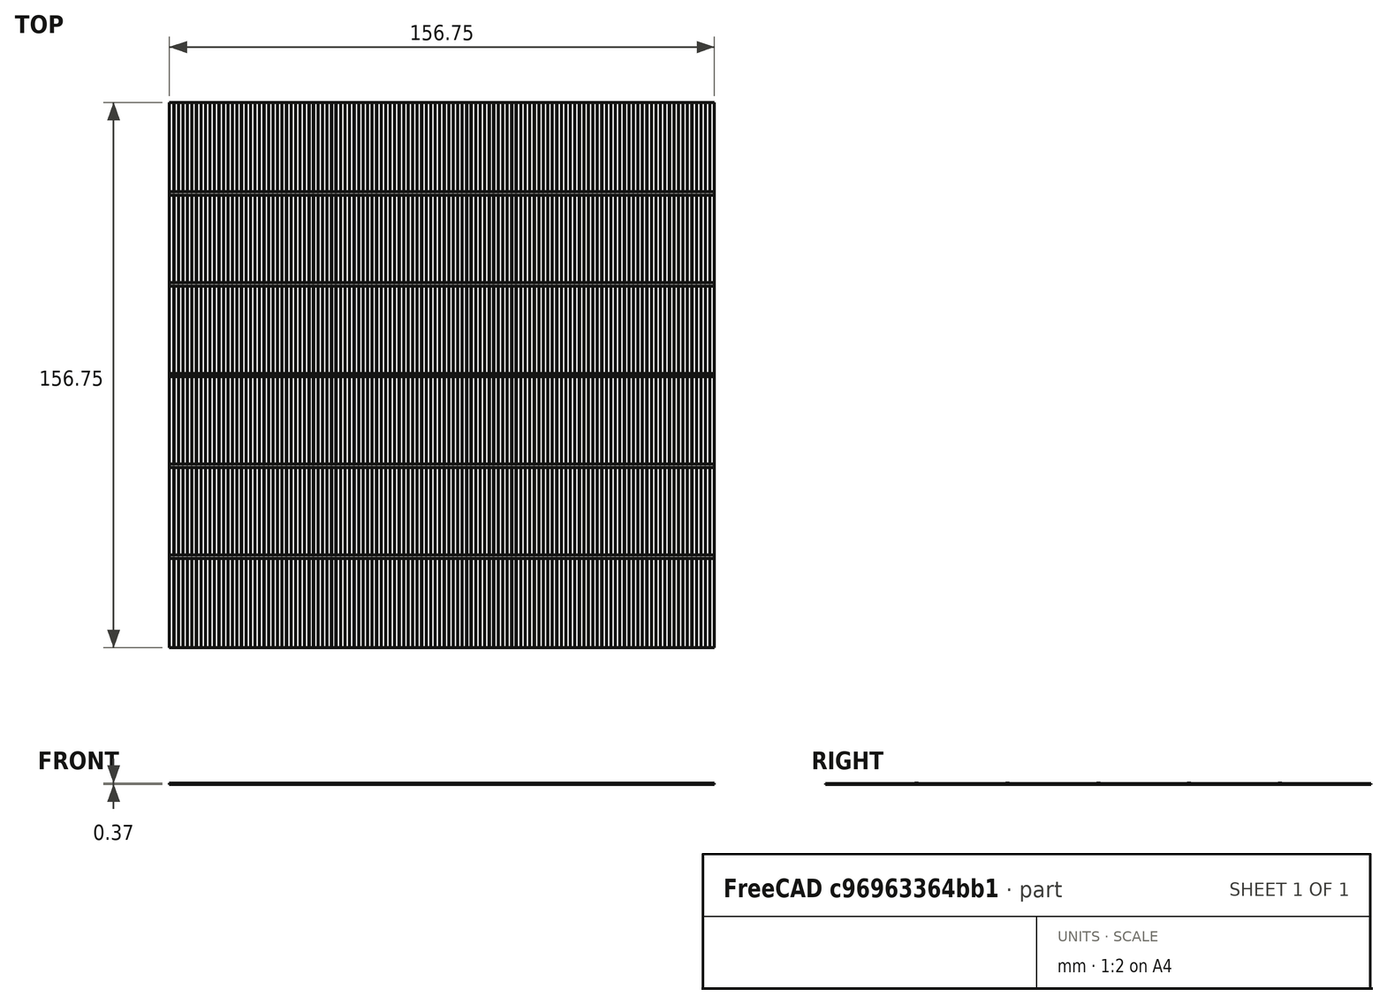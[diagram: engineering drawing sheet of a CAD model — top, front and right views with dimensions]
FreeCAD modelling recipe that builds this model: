
FCSTD DOCUMENT  (FreeCAD 0.19R24276 (Git))
Label: PV_cell
License: All rights reserved
LicenseURL: http://en.wikipedia.org/wiki/All_rights_reserved
objects: Part::Box×128, Part::Feature×6
note: 134 computed .brp shape members not serialized (recipe doc carries the construction recipe); baked Part::Feature solids carry a one-line shape summary decoded from their .brp

FEATURE [Part::Box] Box_Rear_R  label="Box_Rear_R(Box_Rear_R_mat)"
  AttacherType = Attacher::AttachEngine3D
  Height = 1e-05
  Length = 156.75
  Width = 156.75
FEATURE [Part::Feature] Layer_Rear_R  label="Layer_Rear_R(Layer_Rear_R_mat)"
  shape: bbox 156.8 x 156.8 x 2e-07 mm, 1 faces, 0 solids (baked)
FEATURE [Part::Box] Box_Cell  label="Glass_ARC(Box_Cell_mat)"
  AttacherType = Attacher::AttachEngine3D
  Height = 0.17
  Length = 156.75
  Placement = pos=(0,0,1e-05) rot=(0,0,1;0rad)
  Width = 156.75
FEATURE [Part::Box] Box_Front_ARC  label="Box_Front_ARC(Box_Front_ARC_mat)"
  AttacherType = Attacher::AttachEngine3D
  Height = 7.4e-05
  Length = 156.75
  Placement = pos=(0,0,0.17001) rot=(0,0,1;0rad)
  Width = 156.75
FEATURE [Part::Box] Box_Connector_1  label="Box_Connector_1(Box_Connector_mat)"
  AttacherType = Attacher::AttachEngine3D
  Height = 0.2
  Length = 156.75
  Placement = pos=(0,25.625,0.170084) rot=(0,0,1;0rad)
  Width = 1
FEATURE [Part::Box] Box_Connector_2  label="Box_Connector_2(Box_Connector_mat)"
  AttacherType = Attacher::AttachEngine3D
  Height = 0.2
  Length = 156.75
  Placement = pos=(0,51.75,0.170084) rot=(0,0,1;0rad)
  Width = 1
FEATURE [Part::Box] Box_Connector_3  label="Box_Connector_3(Box_Connector_mat)"
  AttacherType = Attacher::AttachEngine3D
  Height = 0.2
  Length = 156.75
  Placement = pos=(0,77.875,0.170084) rot=(0,0,1;0rad)
  Width = 1
FEATURE [Part::Box] Box_Connector_4  label="Box_Connector_4(Box_Connector_mat)"
  AttacherType = Attacher::AttachEngine3D
  Height = 0.2
  Length = 156.75
  Placement = pos=(0,104,0.170084) rot=(0,0,1;0rad)
  Width = 1
FEATURE [Part::Box] Box_Connector_5  label="Box_Connector_5(Box_Connector_mat)"
  AttacherType = Attacher::AttachEngine3D
  Height = 0.2
  Length = 156.75
  Placement = pos=(0,130.125,0.170084) rot=(0,0,1;0rad)
  Width = 1
FEATURE [Part::Box] Box_Finger_1  label="Box_Finger_1(Box_Finger_mat)"
  AttacherType = Attacher::AttachEngine3D
  Height = 0.02
  Length = 0.035
  Placement = pos=(1.27795,0,0.170084) rot=(0,0,1;0rad)
  Width = 156.75
FEATURE [Part::Box] Box_Finger_2  label="Box_Finger_2(Box_Finger_mat)"
  AttacherType = Attacher::AttachEngine3D
  Height = 0.02
  Length = 0.035
  Placement = pos=(2.57341,0,0.170084) rot=(0,0,1;0rad)
  Width = 156.75
FEATURE [Part::Box] Box_Finger_3  label="Box_Finger_3(Box_Finger_mat)"
  AttacherType = Attacher::AttachEngine3D
  Height = 0.02
  Length = 0.035
  Placement = pos=(3.86886,0,0.170084) rot=(0,0,1;0rad)
  Width = 156.75
FEATURE [Part::Box] Box_Finger_4  label="Box_Finger_4(Box_Finger_mat)"
  AttacherType = Attacher::AttachEngine3D
  Height = 0.02
  Length = 0.035
  Placement = pos=(5.16432,0,0.170084) rot=(0,0,1;0rad)
  Width = 156.75
FEATURE [Part::Box] Box_Finger_5  label="Box_Finger_5(Box_Finger_mat)"
  AttacherType = Attacher::AttachEngine3D
  Height = 0.02
  Length = 0.035
  Placement = pos=(6.45977,0,0.170084) rot=(0,0,1;0rad)
  Width = 156.75
FEATURE [Part::Box] Box_Finger_6  label="Box_Finger_6(Box_Finger_mat)"
  AttacherType = Attacher::AttachEngine3D
  Height = 0.02
  Length = 0.035
  Placement = pos=(7.75523,0,0.170084) rot=(0,0,1;0rad)
  Width = 156.75
FEATURE [Part::Box] Box_Finger_7  label="Box_Finger_7(Box_Finger_mat)"
  AttacherType = Attacher::AttachEngine3D
  Height = 0.02
  Length = 0.035
  Placement = pos=(9.05068,0,0.170084) rot=(0,0,1;0rad)
  Width = 156.75
FEATURE [Part::Box] Box_Finger_8  label="Box_Finger_8(Box_Finger_mat)"
  AttacherType = Attacher::AttachEngine3D
  Height = 0.02
  Length = 0.035
  Placement = pos=(10.3461,0,0.170084) rot=(0,0,1;0rad)
  Width = 156.75
FEATURE [Part::Box] Box_Finger_9  label="Box_Finger_9(Box_Finger_mat)"
  AttacherType = Attacher::AttachEngine3D
  Height = 0.02
  Length = 0.035
  Placement = pos=(11.6416,0,0.170084) rot=(0,0,1;0rad)
  Width = 156.75
FEATURE [Part::Box] Box_Finger_10  label="Box_Finger_10(Box_Finger_mat)"
  AttacherType = Attacher::AttachEngine3D
  Height = 0.02
  Length = 0.035
  Placement = pos=(12.937,0,0.170084) rot=(0,0,1;0rad)
  Width = 156.75
FEATURE [Part::Box] Box_Finger_11  label="Box_Finger_11(Box_Finger_mat)"
  AttacherType = Attacher::AttachEngine3D
  Height = 0.02
  Length = 0.035
  Placement = pos=(14.2325,0,0.170084) rot=(0,0,1;0rad)
  Width = 156.75
FEATURE [Part::Box] Box_Finger_12  label="Box_Finger_12(Box_Finger_mat)"
  AttacherType = Attacher::AttachEngine3D
  Height = 0.02
  Length = 0.035
  Placement = pos=(15.528,0,0.170084) rot=(0,0,1;0rad)
  Width = 156.75
FEATURE [Part::Box] Box_Finger_13  label="Box_Finger_13(Box_Finger_mat)"
  AttacherType = Attacher::AttachEngine3D
  Height = 0.02
  Length = 0.035
  Placement = pos=(16.8234,0,0.170084) rot=(0,0,1;0rad)
  Width = 156.75
FEATURE [Part::Box] Box_Finger_14  label="Box_Finger_14(Box_Finger_mat)"
  AttacherType = Attacher::AttachEngine3D
  Height = 0.02
  Length = 0.035
  Placement = pos=(18.1189,0,0.170084) rot=(0,0,1;0rad)
  Width = 156.75
FEATURE [Part::Box] Box_Finger_15  label="Box_Finger_15(Box_Finger_mat)"
  AttacherType = Attacher::AttachEngine3D
  Height = 0.02
  Length = 0.035
  Placement = pos=(19.4143,0,0.170084) rot=(0,0,1;0rad)
  Width = 156.75
FEATURE [Part::Box] Box_Finger_16  label="Box_Finger_16(Box_Finger_mat)"
  AttacherType = Attacher::AttachEngine3D
  Height = 0.02
  Length = 0.035
  Placement = pos=(20.7098,0,0.170084) rot=(0,0,1;0rad)
  Width = 156.75
FEATURE [Part::Box] Box_Finger_17  label="Box_Finger_17(Box_Finger_mat)"
  AttacherType = Attacher::AttachEngine3D
  Height = 0.02
  Length = 0.035
  Placement = pos=(22.0052,0,0.170084) rot=(0,0,1;0rad)
  Width = 156.75
FEATURE [Part::Box] Box_Finger_18  label="Box_Finger_18(Box_Finger_mat)"
  AttacherType = Attacher::AttachEngine3D
  Height = 0.02
  Length = 0.035
  Placement = pos=(23.3007,0,0.170084) rot=(0,0,1;0rad)
  Width = 156.75
FEATURE [Part::Box] Box_Finger_19  label="Box_Finger_19(Box_Finger_mat)"
  AttacherType = Attacher::AttachEngine3D
  Height = 0.02
  Length = 0.035
  Placement = pos=(24.5961,0,0.170084) rot=(0,0,1;0rad)
  Width = 156.75
FEATURE [Part::Box] Box_Finger_20  label="Box_Finger_20(Box_Finger_mat)"
  AttacherType = Attacher::AttachEngine3D
  Height = 0.02
  Length = 0.035
  Placement = pos=(25.8916,0,0.170084) rot=(0,0,1;0rad)
  Width = 156.75
FEATURE [Part::Box] Box_Finger_21  label="Box_Finger_21(Box_Finger_mat)"
  AttacherType = Attacher::AttachEngine3D
  Height = 0.02
  Length = 0.035
  Placement = pos=(27.187,0,0.170084) rot=(0,0,1;0rad)
  Width = 156.75
FEATURE [Part::Box] Box_Finger_22  label="Box_Finger_22(Box_Finger_mat)"
  AttacherType = Attacher::AttachEngine3D
  Height = 0.02
  Length = 0.035
  Placement = pos=(28.4825,0,0.170084) rot=(0,0,1;0rad)
  Width = 156.75
FEATURE [Part::Box] Box_Finger_23  label="Box_Finger_23(Box_Finger_mat)"
  AttacherType = Attacher::AttachEngine3D
  Height = 0.02
  Length = 0.035
  Placement = pos=(29.778,0,0.170084) rot=(0,0,1;0rad)
  Width = 156.75
FEATURE [Part::Box] Box_Finger_24  label="Box_Finger_24(Box_Finger_mat)"
  AttacherType = Attacher::AttachEngine3D
  Height = 0.02
  Length = 0.035
  Placement = pos=(31.0734,0,0.170084) rot=(0,0,1;0rad)
  Width = 156.75
FEATURE [Part::Box] Box_Finger_25  label="Box_Finger_25(Box_Finger_mat)"
  AttacherType = Attacher::AttachEngine3D
  Height = 0.02
  Length = 0.035
  Placement = pos=(32.3689,0,0.170084) rot=(0,0,1;0rad)
  Width = 156.75
FEATURE [Part::Box] Box_Finger_26  label="Box_Finger_26(Box_Finger_mat)"
  AttacherType = Attacher::AttachEngine3D
  Height = 0.02
  Length = 0.035
  Placement = pos=(33.6643,0,0.170084) rot=(0,0,1;0rad)
  Width = 156.75
FEATURE [Part::Box] Box_Finger_27  label="Box_Finger_27(Box_Finger_mat)"
  AttacherType = Attacher::AttachEngine3D
  Height = 0.02
  Length = 0.035
  Placement = pos=(34.9598,0,0.170084) rot=(0,0,1;0rad)
  Width = 156.75
FEATURE [Part::Box] Box_Finger_28  label="Box_Finger_28(Box_Finger_mat)"
  AttacherType = Attacher::AttachEngine3D
  Height = 0.02
  Length = 0.035
  Placement = pos=(36.2552,0,0.170084) rot=(0,0,1;0rad)
  Width = 156.75
FEATURE [Part::Box] Box_Finger_29  label="Box_Finger_29(Box_Finger_mat)"
  AttacherType = Attacher::AttachEngine3D
  Height = 0.02
  Length = 0.035
  Placement = pos=(37.5507,0,0.170084) rot=(0,0,1;0rad)
  Width = 156.75
FEATURE [Part::Box] Box_Finger_30  label="Box_Finger_30(Box_Finger_mat)"
  AttacherType = Attacher::AttachEngine3D
  Height = 0.02
  Length = 0.035
  Placement = pos=(38.8461,0,0.170084) rot=(0,0,1;0rad)
  Width = 156.75
FEATURE [Part::Box] Box_Finger_31  label="Box_Finger_31(Box_Finger_mat)"
  AttacherType = Attacher::AttachEngine3D
  Height = 0.02
  Length = 0.035
  Placement = pos=(40.1416,0,0.170084) rot=(0,0,1;0rad)
  Width = 156.75
FEATURE [Part::Box] Box_Finger_32  label="Box_Finger_32(Box_Finger_mat)"
  AttacherType = Attacher::AttachEngine3D
  Height = 0.02
  Length = 0.035
  Placement = pos=(41.437,0,0.170084) rot=(0,0,1;0rad)
  Width = 156.75
FEATURE [Part::Box] Box_Finger_33  label="Box_Finger_33(Box_Finger_mat)"
  AttacherType = Attacher::AttachEngine3D
  Height = 0.02
  Length = 0.035
  Placement = pos=(42.7325,0,0.170084) rot=(0,0,1;0rad)
  Width = 156.75
FEATURE [Part::Box] Box_Finger_34  label="Box_Finger_34(Box_Finger_mat)"
  AttacherType = Attacher::AttachEngine3D
  Height = 0.02
  Length = 0.035
  Placement = pos=(44.028,0,0.170084) rot=(0,0,1;0rad)
  Width = 156.75
FEATURE [Part::Box] Box_Finger_35  label="Box_Finger_35(Box_Finger_mat)"
  AttacherType = Attacher::AttachEngine3D
  Height = 0.02
  Length = 0.035
  Placement = pos=(45.3234,0,0.170084) rot=(0,0,1;0rad)
  Width = 156.75
FEATURE [Part::Box] Box_Finger_36  label="Box_Finger_36(Box_Finger_mat)"
  AttacherType = Attacher::AttachEngine3D
  Height = 0.02
  Length = 0.035
  Placement = pos=(46.6189,0,0.170084) rot=(0,0,1;0rad)
  Width = 156.75
FEATURE [Part::Box] Box_Finger_37  label="Box_Finger_37(Box_Finger_mat)"
  AttacherType = Attacher::AttachEngine3D
  Height = 0.02
  Length = 0.035
  Placement = pos=(47.9143,0,0.170084) rot=(0,0,1;0rad)
  Width = 156.75
FEATURE [Part::Box] Box_Finger_38  label="Box_Finger_38(Box_Finger_mat)"
  AttacherType = Attacher::AttachEngine3D
  Height = 0.02
  Length = 0.035
  Placement = pos=(49.2098,0,0.170084) rot=(0,0,1;0rad)
  Width = 156.75
FEATURE [Part::Box] Box_Finger_39  label="Box_Finger_39(Box_Finger_mat)"
  AttacherType = Attacher::AttachEngine3D
  Height = 0.02
  Length = 0.035
  Placement = pos=(50.5052,0,0.170084) rot=(0,0,1;0rad)
  Width = 156.75
FEATURE [Part::Box] Box_Finger_40  label="Box_Finger_40(Box_Finger_mat)"
  AttacherType = Attacher::AttachEngine3D
  Height = 0.02
  Length = 0.035
  Placement = pos=(51.8007,0,0.170084) rot=(0,0,1;0rad)
  Width = 156.75
FEATURE [Part::Box] Box_Finger_41  label="Box_Finger_41(Box_Finger_mat)"
  AttacherType = Attacher::AttachEngine3D
  Height = 0.02
  Length = 0.035
  Placement = pos=(53.0961,0,0.170084) rot=(0,0,1;0rad)
  Width = 156.75
FEATURE [Part::Box] Box_Finger_42  label="Box_Finger_42(Box_Finger_mat)"
  AttacherType = Attacher::AttachEngine3D
  Height = 0.02
  Length = 0.035
  Placement = pos=(54.3916,0,0.170084) rot=(0,0,1;0rad)
  Width = 156.75
FEATURE [Part::Box] Box_Finger_43  label="Box_Finger_43(Box_Finger_mat)"
  AttacherType = Attacher::AttachEngine3D
  Height = 0.02
  Length = 0.035
  Placement = pos=(55.687,0,0.170084) rot=(0,0,1;0rad)
  Width = 156.75
FEATURE [Part::Box] Box_Finger_44  label="Box_Finger_44(Box_Finger_mat)"
  AttacherType = Attacher::AttachEngine3D
  Height = 0.02
  Length = 0.035
  Placement = pos=(56.9825,0,0.170084) rot=(0,0,1;0rad)
  Width = 156.75
FEATURE [Part::Box] Box_Finger_45  label="Box_Finger_45(Box_Finger_mat)"
  AttacherType = Attacher::AttachEngine3D
  Height = 0.02
  Length = 0.035
  Placement = pos=(58.278,0,0.170084) rot=(0,0,1;0rad)
  Width = 156.75
FEATURE [Part::Box] Box_Finger_46  label="Box_Finger_46(Box_Finger_mat)"
  AttacherType = Attacher::AttachEngine3D
  Height = 0.02
  Length = 0.035
  Placement = pos=(59.5734,0,0.170084) rot=(0,0,1;0rad)
  Width = 156.75
FEATURE [Part::Box] Box_Finger_47  label="Box_Finger_47(Box_Finger_mat)"
  AttacherType = Attacher::AttachEngine3D
  Height = 0.02
  Length = 0.035
  Placement = pos=(60.8689,0,0.170084) rot=(0,0,1;0rad)
  Width = 156.75
FEATURE [Part::Box] Box_Finger_48  label="Box_Finger_48(Box_Finger_mat)"
  AttacherType = Attacher::AttachEngine3D
  Height = 0.02
  Length = 0.035
  Placement = pos=(62.1643,0,0.170084) rot=(0,0,1;0rad)
  Width = 156.75
FEATURE [Part::Box] Box_Finger_49  label="Box_Finger_49(Box_Finger_mat)"
  AttacherType = Attacher::AttachEngine3D
  Height = 0.02
  Length = 0.035
  Placement = pos=(63.4598,0,0.170084) rot=(0,0,1;0rad)
  Width = 156.75
FEATURE [Part::Box] Box_Finger_50  label="Box_Finger_50(Box_Finger_mat)"
  AttacherType = Attacher::AttachEngine3D
  Height = 0.02
  Length = 0.035
  Placement = pos=(64.7552,0,0.170084) rot=(0,0,1;0rad)
  Width = 156.75
FEATURE [Part::Box] Box_Finger_51  label="Box_Finger_51(Box_Finger_mat)"
  AttacherType = Attacher::AttachEngine3D
  Height = 0.02
  Length = 0.035
  Placement = pos=(66.0507,0,0.170084) rot=(0,0,1;0rad)
  Width = 156.75
FEATURE [Part::Box] Box_Finger_52  label="Box_Finger_52(Box_Finger_mat)"
  AttacherType = Attacher::AttachEngine3D
  Height = 0.02
  Length = 0.035
  Placement = pos=(67.3461,0,0.170084) rot=(0,0,1;0rad)
  Width = 156.75
FEATURE [Part::Box] Box_Finger_53  label="Box_Finger_53(Box_Finger_mat)"
  AttacherType = Attacher::AttachEngine3D
  Height = 0.02
  Length = 0.035
  Placement = pos=(68.6416,0,0.170084) rot=(0,0,1;0rad)
  Width = 156.75
FEATURE [Part::Box] Box_Finger_54  label="Box_Finger_54(Box_Finger_mat)"
  AttacherType = Attacher::AttachEngine3D
  Height = 0.02
  Length = 0.035
  Placement = pos=(69.937,0,0.170084) rot=(0,0,1;0rad)
  Width = 156.75
FEATURE [Part::Box] Box_Finger_55  label="Box_Finger_55(Box_Finger_mat)"
  AttacherType = Attacher::AttachEngine3D
  Height = 0.02
  Length = 0.035
  Placement = pos=(71.2325,0,0.170084) rot=(0,0,1;0rad)
  Width = 156.75
FEATURE [Part::Box] Box_Finger_56  label="Box_Finger_56(Box_Finger_mat)"
  AttacherType = Attacher::AttachEngine3D
  Height = 0.02
  Length = 0.035
  Placement = pos=(72.528,0,0.170084) rot=(0,0,1;0rad)
  Width = 156.75
FEATURE [Part::Box] Box_Finger_57  label="Box_Finger_57(Box_Finger_mat)"
  AttacherType = Attacher::AttachEngine3D
  Height = 0.02
  Length = 0.035
  Placement = pos=(73.8234,0,0.170084) rot=(0,0,1;0rad)
  Width = 156.75
FEATURE [Part::Box] Box_Finger_58  label="Box_Finger_58(Box_Finger_mat)"
  AttacherType = Attacher::AttachEngine3D
  Height = 0.02
  Length = 0.035
  Placement = pos=(75.1189,0,0.170084) rot=(0,0,1;0rad)
  Width = 156.75
FEATURE [Part::Box] Box_Finger_59  label="Box_Finger_59(Box_Finger_mat)"
  AttacherType = Attacher::AttachEngine3D
  Height = 0.02
  Length = 0.035
  Placement = pos=(76.4143,0,0.170084) rot=(0,0,1;0rad)
  Width = 156.75
FEATURE [Part::Box] Box_Finger_60  label="Box_Finger_60(Box_Finger_mat)"
  AttacherType = Attacher::AttachEngine3D
  Height = 0.02
  Length = 0.035
  Placement = pos=(77.7098,0,0.170084) rot=(0,0,1;0rad)
  Width = 156.75
FEATURE [Part::Box] Box_Finger_61  label="Box_Finger_61(Box_Finger_mat)"
  AttacherType = Attacher::AttachEngine3D
  Height = 0.02
  Length = 0.035
  Placement = pos=(79.0052,0,0.170084) rot=(0,0,1;0rad)
  Width = 156.75
FEATURE [Part::Box] Box_Finger_62  label="Box_Finger_62(Box_Finger_mat)"
  AttacherType = Attacher::AttachEngine3D
  Height = 0.02
  Length = 0.035
  Placement = pos=(80.3007,0,0.170084) rot=(0,0,1;0rad)
  Width = 156.75
FEATURE [Part::Box] Box_Finger_63  label="Box_Finger_63(Box_Finger_mat)"
  AttacherType = Attacher::AttachEngine3D
  Height = 0.02
  Length = 0.035
  Placement = pos=(81.5961,0,0.170084) rot=(0,0,1;0rad)
  Width = 156.75
FEATURE [Part::Box] Box_Finger_64  label="Box_Finger_64(Box_Finger_mat)"
  AttacherType = Attacher::AttachEngine3D
  Height = 0.02
  Length = 0.035
  Placement = pos=(82.8916,0,0.170084) rot=(0,0,1;0rad)
  Width = 156.75
FEATURE [Part::Box] Box_Finger_65  label="Box_Finger_65(Box_Finger_mat)"
  AttacherType = Attacher::AttachEngine3D
  Height = 0.02
  Length = 0.035
  Placement = pos=(84.187,0,0.170084) rot=(0,0,1;0rad)
  Width = 156.75
FEATURE [Part::Box] Box_Finger_66  label="Box_Finger_66(Box_Finger_mat)"
  AttacherType = Attacher::AttachEngine3D
  Height = 0.02
  Length = 0.035
  Placement = pos=(85.4825,0,0.170084) rot=(0,0,1;0rad)
  Width = 156.75
FEATURE [Part::Box] Box_Finger_67  label="Box_Finger_67(Box_Finger_mat)"
  AttacherType = Attacher::AttachEngine3D
  Height = 0.02
  Length = 0.035
  Placement = pos=(86.778,0,0.170084) rot=(0,0,1;0rad)
  Width = 156.75
FEATURE [Part::Box] Box_Finger_68  label="Box_Finger_68(Box_Finger_mat)"
  AttacherType = Attacher::AttachEngine3D
  Height = 0.02
  Length = 0.035
  Placement = pos=(88.0734,0,0.170084) rot=(0,0,1;0rad)
  Width = 156.75
FEATURE [Part::Box] Box_Finger_69  label="Box_Finger_69(Box_Finger_mat)"
  AttacherType = Attacher::AttachEngine3D
  Height = 0.02
  Length = 0.035
  Placement = pos=(89.3689,0,0.170084) rot=(0,0,1;0rad)
  Width = 156.75
FEATURE [Part::Box] Box_Finger_70  label="Box_Finger_70(Box_Finger_mat)"
  AttacherType = Attacher::AttachEngine3D
  Height = 0.02
  Length = 0.035
  Placement = pos=(90.6643,0,0.170084) rot=(0,0,1;0rad)
  Width = 156.75
FEATURE [Part::Box] Box_Finger_71  label="Box_Finger_71(Box_Finger_mat)"
  AttacherType = Attacher::AttachEngine3D
  Height = 0.02
  Length = 0.035
  Placement = pos=(91.9598,0,0.170084) rot=(0,0,1;0rad)
  Width = 156.75
FEATURE [Part::Box] Box_Finger_72  label="Box_Finger_72(Box_Finger_mat)"
  AttacherType = Attacher::AttachEngine3D
  Height = 0.02
  Length = 0.035
  Placement = pos=(93.2552,0,0.170084) rot=(0,0,1;0rad)
  Width = 156.75
FEATURE [Part::Box] Box_Finger_73  label="Box_Finger_73(Box_Finger_mat)"
  AttacherType = Attacher::AttachEngine3D
  Height = 0.02
  Length = 0.035
  Placement = pos=(94.5507,0,0.170084) rot=(0,0,1;0rad)
  Width = 156.75
FEATURE [Part::Box] Box_Finger_74  label="Box_Finger_74(Box_Finger_mat)"
  AttacherType = Attacher::AttachEngine3D
  Height = 0.02
  Length = 0.035
  Placement = pos=(95.8461,0,0.170084) rot=(0,0,1;0rad)
  Width = 156.75
FEATURE [Part::Box] Box_Finger_75  label="Box_Finger_75(Box_Finger_mat)"
  AttacherType = Attacher::AttachEngine3D
  Height = 0.02
  Length = 0.035
  Placement = pos=(97.1416,0,0.170084) rot=(0,0,1;0rad)
  Width = 156.75
FEATURE [Part::Box] Box_Finger_76  label="Box_Finger_76(Box_Finger_mat)"
  AttacherType = Attacher::AttachEngine3D
  Height = 0.02
  Length = 0.035
  Placement = pos=(98.437,0,0.170084) rot=(0,0,1;0rad)
  Width = 156.75
FEATURE [Part::Box] Box_Finger_77  label="Box_Finger_77(Box_Finger_mat)"
  AttacherType = Attacher::AttachEngine3D
  Height = 0.02
  Length = 0.035
  Placement = pos=(99.7325,0,0.170084) rot=(0,0,1;0rad)
  Width = 156.75
FEATURE [Part::Box] Box_Finger_78  label="Box_Finger_78(Box_Finger_mat)"
  AttacherType = Attacher::AttachEngine3D
  Height = 0.02
  Length = 0.035
  Placement = pos=(101.028,0,0.170084) rot=(0,0,1;0rad)
  Width = 156.75
FEATURE [Part::Box] Box_Finger_79  label="Box_Finger_79(Box_Finger_mat)"
  AttacherType = Attacher::AttachEngine3D
  Height = 0.02
  Length = 0.035
  Placement = pos=(102.323,0,0.170084) rot=(0,0,1;0rad)
  Width = 156.75
FEATURE [Part::Box] Box_Finger_80  label="Box_Finger_80(Box_Finger_mat)"
  AttacherType = Attacher::AttachEngine3D
  Height = 0.02
  Length = 0.035
  Placement = pos=(103.619,0,0.170084) rot=(0,0,1;0rad)
  Width = 156.75
FEATURE [Part::Box] Box_Finger_81  label="Box_Finger_81(Box_Finger_mat)"
  AttacherType = Attacher::AttachEngine3D
  Height = 0.02
  Length = 0.035
  Placement = pos=(104.914,0,0.170084) rot=(0,0,1;0rad)
  Width = 156.75
FEATURE [Part::Box] Box_Finger_82  label="Box_Finger_82(Box_Finger_mat)"
  AttacherType = Attacher::AttachEngine3D
  Height = 0.02
  Length = 0.035
  Placement = pos=(106.21,0,0.170084) rot=(0,0,1;0rad)
  Width = 156.75
FEATURE [Part::Box] Box_Finger_83  label="Box_Finger_83(Box_Finger_mat)"
  AttacherType = Attacher::AttachEngine3D
  Height = 0.02
  Length = 0.035
  Placement = pos=(107.505,0,0.170084) rot=(0,0,1;0rad)
  Width = 156.75
FEATURE [Part::Box] Box_Finger_84  label="Box_Finger_84(Box_Finger_mat)"
  AttacherType = Attacher::AttachEngine3D
  Height = 0.02
  Length = 0.035
  Placement = pos=(108.801,0,0.170084) rot=(0,0,1;0rad)
  Width = 156.75
FEATURE [Part::Box] Box_Finger_85  label="Box_Finger_85(Box_Finger_mat)"
  AttacherType = Attacher::AttachEngine3D
  Height = 0.02
  Length = 0.035
  Placement = pos=(110.096,0,0.170084) rot=(0,0,1;0rad)
  Width = 156.75
FEATURE [Part::Box] Box_Finger_86  label="Box_Finger_86(Box_Finger_mat)"
  AttacherType = Attacher::AttachEngine3D
  Height = 0.02
  Length = 0.035
  Placement = pos=(111.392,0,0.170084) rot=(0,0,1;0rad)
  Width = 156.75
FEATURE [Part::Box] Box_Finger_87  label="Box_Finger_87(Box_Finger_mat)"
  AttacherType = Attacher::AttachEngine3D
  Height = 0.02
  Length = 0.035
  Placement = pos=(112.687,0,0.170084) rot=(0,0,1;0rad)
  Width = 156.75
FEATURE [Part::Box] Box_Finger_88  label="Box_Finger_88(Box_Finger_mat)"
  AttacherType = Attacher::AttachEngine3D
  Height = 0.02
  Length = 0.035
  Placement = pos=(113.983,0,0.170084) rot=(0,0,1;0rad)
  Width = 156.75
FEATURE [Part::Box] Box_Finger_89  label="Box_Finger_89(Box_Finger_mat)"
  AttacherType = Attacher::AttachEngine3D
  Height = 0.02
  Length = 0.035
  Placement = pos=(115.278,0,0.170084) rot=(0,0,1;0rad)
  Width = 156.75
FEATURE [Part::Box] Box_Finger_90  label="Box_Finger_90(Box_Finger_mat)"
  AttacherType = Attacher::AttachEngine3D
  Height = 0.02
  Length = 0.035
  Placement = pos=(116.573,0,0.170084) rot=(0,0,1;0rad)
  Width = 156.75
FEATURE [Part::Box] Box_Finger_91  label="Box_Finger_91(Box_Finger_mat)"
  AttacherType = Attacher::AttachEngine3D
  Height = 0.02
  Length = 0.035
  Placement = pos=(117.869,0,0.170084) rot=(0,0,1;0rad)
  Width = 156.75
FEATURE [Part::Box] Box_Finger_92  label="Box_Finger_92(Box_Finger_mat)"
  AttacherType = Attacher::AttachEngine3D
  Height = 0.02
  Length = 0.035
  Placement = pos=(119.164,0,0.170084) rot=(0,0,1;0rad)
  Width = 156.75
FEATURE [Part::Box] Box_Finger_93  label="Box_Finger_93(Box_Finger_mat)"
  AttacherType = Attacher::AttachEngine3D
  Height = 0.02
  Length = 0.035
  Placement = pos=(120.46,0,0.170084) rot=(0,0,1;0rad)
  Width = 156.75
FEATURE [Part::Box] Box_Finger_94  label="Box_Finger_94(Box_Finger_mat)"
  AttacherType = Attacher::AttachEngine3D
  Height = 0.02
  Length = 0.035
  Placement = pos=(121.755,0,0.170084) rot=(0,0,1;0rad)
  Width = 156.75
FEATURE [Part::Box] Box_Finger_95  label="Box_Finger_95(Box_Finger_mat)"
  AttacherType = Attacher::AttachEngine3D
  Height = 0.02
  Length = 0.035
  Placement = pos=(123.051,0,0.170084) rot=(0,0,1;0rad)
  Width = 156.75
FEATURE [Part::Box] Box_Finger_96  label="Box_Finger_96(Box_Finger_mat)"
  AttacherType = Attacher::AttachEngine3D
  Height = 0.02
  Length = 0.035
  Placement = pos=(124.346,0,0.170084) rot=(0,0,1;0rad)
  Width = 156.75
FEATURE [Part::Box] Box_Finger_97  label="Box_Finger_97(Box_Finger_mat)"
  AttacherType = Attacher::AttachEngine3D
  Height = 0.02
  Length = 0.035
  Placement = pos=(125.642,0,0.170084) rot=(0,0,1;0rad)
  Width = 156.75
FEATURE [Part::Box] Box_Finger_98  label="Box_Finger_98(Box_Finger_mat)"
  AttacherType = Attacher::AttachEngine3D
  Height = 0.02
  Length = 0.035
  Placement = pos=(126.937,0,0.170084) rot=(0,0,1;0rad)
  Width = 156.75
FEATURE [Part::Box] Box_Finger_99  label="Box_Finger_99(Box_Finger_mat)"
  AttacherType = Attacher::AttachEngine3D
  Height = 0.02
  Length = 0.035
  Placement = pos=(128.232,0,0.170084) rot=(0,0,1;0rad)
  Width = 156.75
FEATURE [Part::Box] Box_Finger_100  label="Box_Finger_100(Box_Finger_mat)"
  AttacherType = Attacher::AttachEngine3D
  Height = 0.02
  Length = 0.035
  Placement = pos=(129.528,0,0.170084) rot=(0,0,1;0rad)
  Width = 156.75
FEATURE [Part::Box] Box_Finger_101  label="Box_Finger_101(Box_Finger_mat)"
  AttacherType = Attacher::AttachEngine3D
  Height = 0.02
  Length = 0.035
  Placement = pos=(130.823,0,0.170084) rot=(0,0,1;0rad)
  Width = 156.75
FEATURE [Part::Box] Box_Finger_102  label="Box_Finger_102(Box_Finger_mat)"
  AttacherType = Attacher::AttachEngine3D
  Height = 0.02
  Length = 0.035
  Placement = pos=(132.119,0,0.170084) rot=(0,0,1;0rad)
  Width = 156.75
FEATURE [Part::Box] Box_Finger_103  label="Box_Finger_103(Box_Finger_mat)"
  AttacherType = Attacher::AttachEngine3D
  Height = 0.02
  Length = 0.035
  Placement = pos=(133.414,0,0.170084) rot=(0,0,1;0rad)
  Width = 156.75
FEATURE [Part::Box] Box_Finger_104  label="Box_Finger_104(Box_Finger_mat)"
  AttacherType = Attacher::AttachEngine3D
  Height = 0.02
  Length = 0.035
  Placement = pos=(134.71,0,0.170084) rot=(0,0,1;0rad)
  Width = 156.75
FEATURE [Part::Box] Box_Finger_105  label="Box_Finger_105(Box_Finger_mat)"
  AttacherType = Attacher::AttachEngine3D
  Height = 0.02
  Length = 0.035
  Placement = pos=(136.005,0,0.170084) rot=(0,0,1;0rad)
  Width = 156.75
FEATURE [Part::Box] Box_Finger_106  label="Box_Finger_106(Box_Finger_mat)"
  AttacherType = Attacher::AttachEngine3D
  Height = 0.02
  Length = 0.035
  Placement = pos=(137.301,0,0.170084) rot=(0,0,1;0rad)
  Width = 156.75
FEATURE [Part::Box] Box_Finger_107  label="Box_Finger_107(Box_Finger_mat)"
  AttacherType = Attacher::AttachEngine3D
  Height = 0.02
  Length = 0.035
  Placement = pos=(138.596,0,0.170084) rot=(0,0,1;0rad)
  Width = 156.75
FEATURE [Part::Box] Box_Finger_108  label="Box_Finger_108(Box_Finger_mat)"
  AttacherType = Attacher::AttachEngine3D
  Height = 0.02
  Length = 0.035
  Placement = pos=(139.892,0,0.170084) rot=(0,0,1;0rad)
  Width = 156.75
FEATURE [Part::Box] Box_Finger_109  label="Box_Finger_109(Box_Finger_mat)"
  AttacherType = Attacher::AttachEngine3D
  Height = 0.02
  Length = 0.035
  Placement = pos=(141.187,0,0.170084) rot=(0,0,1;0rad)
  Width = 156.75
FEATURE [Part::Box] Box_Finger_110  label="Box_Finger_110(Box_Finger_mat)"
  AttacherType = Attacher::AttachEngine3D
  Height = 0.02
  Length = 0.035
  Placement = pos=(142.482,0,0.170084) rot=(0,0,1;0rad)
  Width = 156.75
FEATURE [Part::Box] Box_Finger_111  label="Box_Finger_111(Box_Finger_mat)"
  AttacherType = Attacher::AttachEngine3D
  Height = 0.02
  Length = 0.035
  Placement = pos=(143.778,0,0.170084) rot=(0,0,1;0rad)
  Width = 156.75
FEATURE [Part::Box] Box_Finger_112  label="Box_Finger_112(Box_Finger_mat)"
  AttacherType = Attacher::AttachEngine3D
  Height = 0.02
  Length = 0.035
  Placement = pos=(145.073,0,0.170084) rot=(0,0,1;0rad)
  Width = 156.75
FEATURE [Part::Box] Box_Finger_113  label="Box_Finger_113(Box_Finger_mat)"
  AttacherType = Attacher::AttachEngine3D
  Height = 0.02
  Length = 0.035
  Placement = pos=(146.369,0,0.170084) rot=(0,0,1;0rad)
  Width = 156.75
FEATURE [Part::Box] Box_Finger_114  label="Box_Finger_114(Box_Finger_mat)"
  AttacherType = Attacher::AttachEngine3D
  Height = 0.02
  Length = 0.035
  Placement = pos=(147.664,0,0.170084) rot=(0,0,1;0rad)
  Width = 156.75
FEATURE [Part::Box] Box_Finger_115  label="Box_Finger_115(Box_Finger_mat)"
  AttacherType = Attacher::AttachEngine3D
  Height = 0.02
  Length = 0.035
  Placement = pos=(148.96,0,0.170084) rot=(0,0,1;0rad)
  Width = 156.75
FEATURE [Part::Box] Box_Finger_116  label="Box_Finger_116(Box_Finger_mat)"
  AttacherType = Attacher::AttachEngine3D
  Height = 0.02
  Length = 0.035
  Placement = pos=(150.255,0,0.170084) rot=(0,0,1;0rad)
  Width = 156.75
FEATURE [Part::Box] Box_Finger_117  label="Box_Finger_117(Box_Finger_mat)"
  AttacherType = Attacher::AttachEngine3D
  Height = 0.02
  Length = 0.035
  Placement = pos=(151.551,0,0.170084) rot=(0,0,1;0rad)
  Width = 156.75
FEATURE [Part::Box] Box_Finger_118  label="Box_Finger_118(Box_Finger_mat)"
  AttacherType = Attacher::AttachEngine3D
  Height = 0.02
  Length = 0.035
  Placement = pos=(152.846,0,0.170084) rot=(0,0,1;0rad)
  Width = 156.75
FEATURE [Part::Box] Box_Finger_119  label="Box_Finger_119(Box_Finger_mat)"
  AttacherType = Attacher::AttachEngine3D
  Height = 0.02
  Length = 0.035
  Placement = pos=(154.142,0,0.170084) rot=(0,0,1;0rad)
  Width = 156.75
FEATURE [Part::Box] Box_Finger_120  label="Box_Finger_120(Box_Finger_mat)"
  AttacherType = Attacher::AttachEngine3D
  Height = 0.02
  Length = 0.035
  Placement = pos=(155.437,0,0.170084) rot=(0,0,1;0rad)
  Width = 156.75
FEATURE [Part::Feature] Trans_Abs  label="Trans_Abs(Trans_Abs)"
  Placement = pos=(0,0,0.370184) rot=(0,0,1;0rad)
  shape: bbox 156.8 x 156.8 x 2e-07 mm, 1 faces, 0 solids (baked)
FEATURE [Part::Feature] Mirror_1  label="Mirror_1(Mirror)"
  shape: bbox 156.8 x 2e-07 x 0.3702 mm, 1 faces, 0 solids (baked)
FEATURE [Part::Feature] Mirror_2  label="Mirror_2(Mirror)"
  Placement = pos=(0,156.75,0) rot=(0,0,1;0rad)
  shape: bbox 156.8 x 2e-07 x 0.3702 mm, 1 faces, 0 solids (baked)
FEATURE [Part::Feature] Mirror_3  label="Mirror_3(Mirror)"
  shape: bbox 2e-07 x 156.8 x 0.3702 mm, 1 faces, 0 solids (baked)
FEATURE [Part::Feature] Mirror_4  label="Mirror_4(Mirror)"
  Placement = pos=(-156.75,0,0) rot=(0,0,1;0rad)
  shape: bbox 2e-07 x 156.8 x 0.3702 mm, 1 faces, 0 solids (baked)
